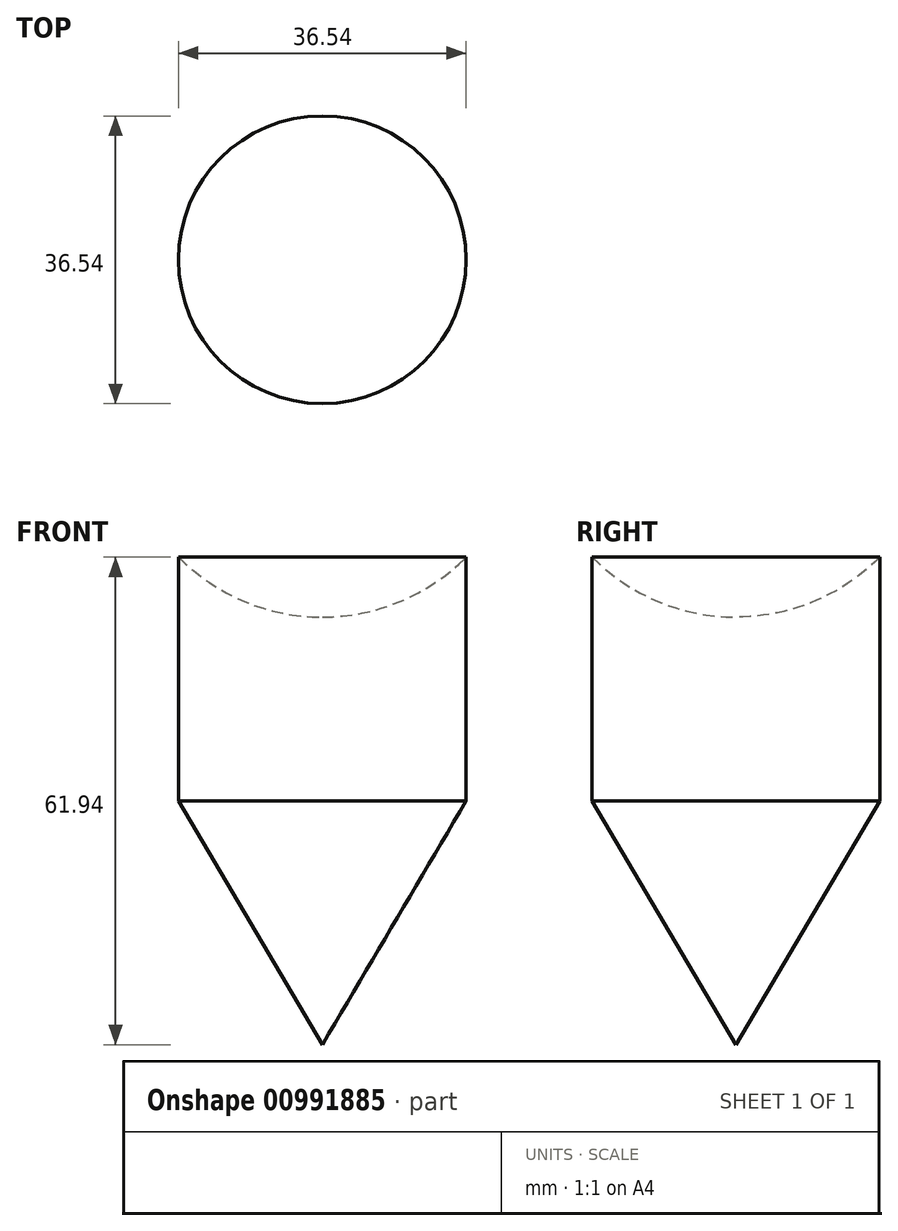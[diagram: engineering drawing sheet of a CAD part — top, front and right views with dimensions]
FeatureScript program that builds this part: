
annotation { "Feature Type Name" : "Feature", "Feature Type Description" : "" }
export const myFeature = defineFeature(function(context is Context, id is Id, definition is map)
    precondition{}
    {
        {
            var Q0;
            Q0=qCreatedBy(makeId("Right.planeOp"),FACE);
            var sketch = newSketch(context, id + "F0", { "sketchPlane" : qUnion([Q0])});
            skLineSegment(sketch, "E0", {"start": v(0, 0) * mm, "end": v(0, 54.32) * mm});
            skLineSegment(sketch, "E1", {"start": v(18.27, 61.94) * mm, "end": v(18.27, 36.54) * mm});
            skLineSegment(sketch, "E2", {"start": v(18.27, 36.54) * mm, "end": v(18.27, 30.97) * mm});
            skPoint(sketch, "E2.endSnap0", {"position": v(0, 30.97) * mm});
            skLineSegment(sketch, "E3", {"start": v(18.27, 30.97) * mm, "end": v(0, 0) * mm});
            skArc(sketch, "E4", {"start": v(0, 54.32) * mm, "mid": v(9.9, 56.3) * mm, "end": v(18.27, 61.94) * mm});
            skPoint(sketch, "E5.MirrorCS.end.orphan", {"position": v(-18.27, 61.94) * mm});
            skPoint(sketch, "E5.MirrorCS.start.orphan", {"position": v(0, 61.94) * mm});
            skSolve(sketch);
        }
        {
            var Q0;
            Q0 = qSketchRegion(id + "F0", true);
            var Q1;
            Q1=sQuery(id+"F0.wireOp",EDGE,"E0");
            revolve(context, id + "F1", {"surfaceOperationType" : NewSurfaceOperationType.NEW, "entities" : qUnion([Q0]), "axis" : qUnion([Q1]), "revolveType" : RevolveType.FULL});
        }
    });
